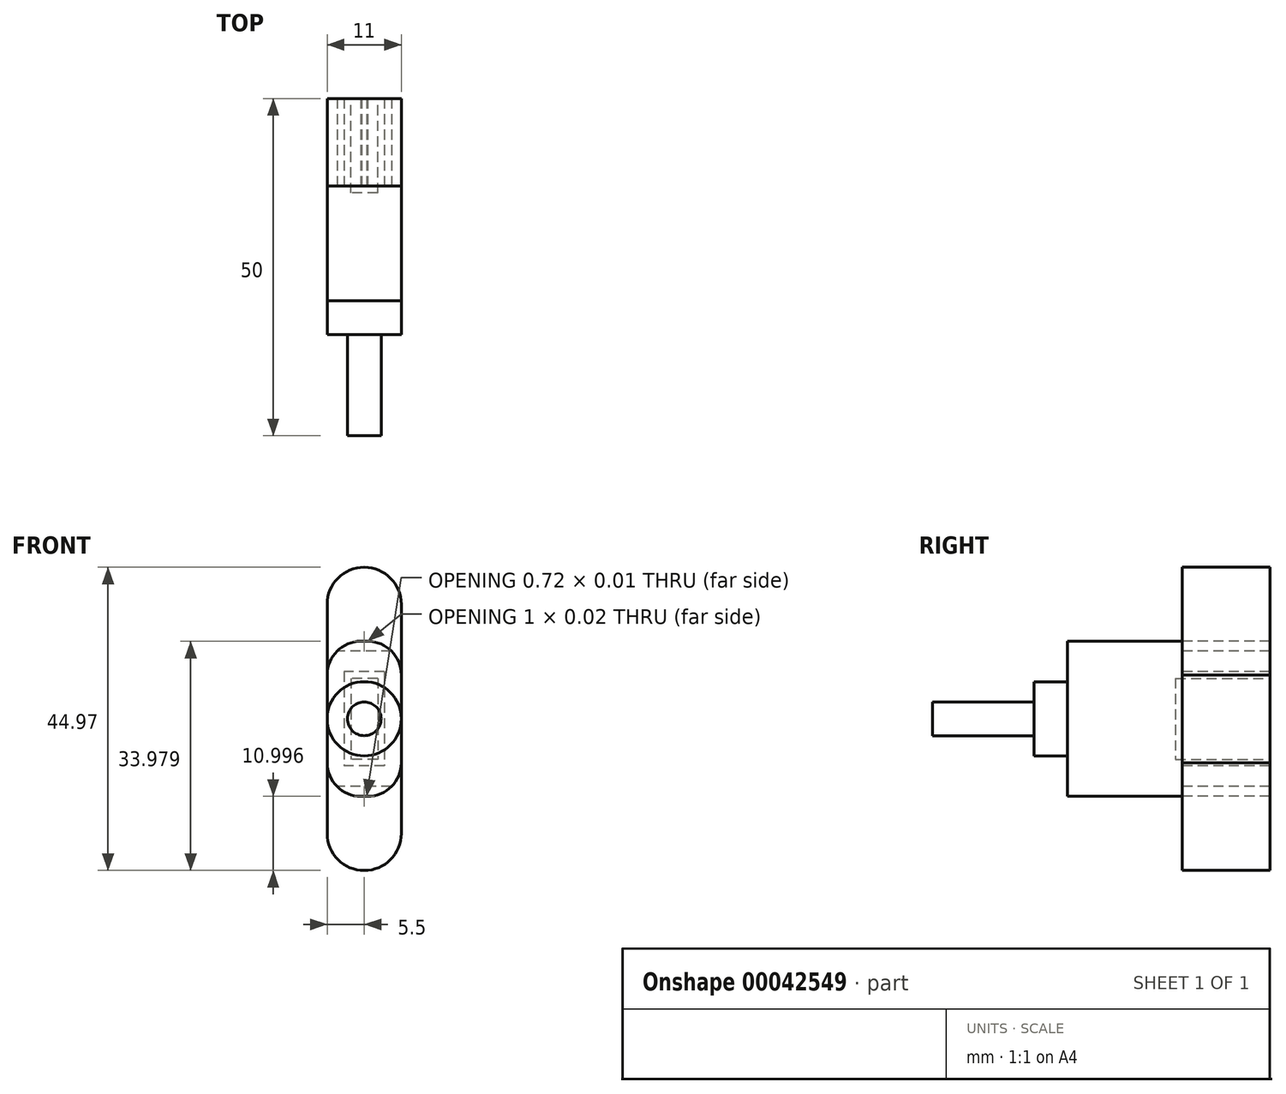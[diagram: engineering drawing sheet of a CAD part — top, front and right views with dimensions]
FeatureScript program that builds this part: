
annotation { "Feature Type Name" : "Feature", "Feature Type Description" : "" }
export const myFeature = defineFeature(function(context is Context, id is Id, definition is map)
    precondition{}
    {
        {
            var Q0;
            Q0=qCreatedBy(makeId("Front.planeOp"),FACE);
            var sketch = newSketch(context, id + "F0", { "sketchPlane" : qUnion([Q0])});
            skCircle(sketch, "E0", {"center": v(0, 0) * mm, "radius": 5.5 * mm});
            skSolve(sketch);
        }
        {
            var Q0;
            Q0 = qSketchRegion(id + "F0", true);
            extrude(context, id + "F1", {"entities" : qUnion([Q0]), "depth" : 5 * mm});
        }
        {
            var Q0;
            Q0=makeQuery(id+"F1.opExtrude","CAP_FACE",FACE,{"disambiguationData":[OSD([sQuery(id+"F0.wireOp",EDGE,"E0")])],"isStart":false});
            var sketch = newSketch(context, id + "F2", { "sketchPlane" : qUnion([Q0])});
            skCircle(sketch, "E1", {"center": v(0, 0) * mm, "radius": 2.5 * mm});
            skSolve(sketch);
        }
        {
            var Q0;
            Q0 = qSketchRegion(id + "F2", true);
            extrude(context, id + "F3", {"entities" : qUnion([Q0]), "operationType" : NewBodyOperationType.ADD, "depth" : 15 * mm});
        }
        {
            var Q0;
            Q0=makeQuery(id+"F1.opExtrude","CAP_FACE",FACE,{"disambiguationData":[OSD([sQuery(id+"F0.wireOp",EDGE,"E0")])],"isStart":true});
            var sketch = newSketch(context, id + "F4", { "sketchPlane" : qUnion([Q0])});
            skLineSegment(sketch, "E2", {"start": v(0, 0) * mm, "end": v(5.5, 0) * mm});
            skLineSegment(sketch, "E3", {"start": v(-5.5, 0) * mm, "end": v(0, 0) * mm});
            skLineSegment(sketch, "E4", {"start": v(0, 0) * mm, "end": v(0, 5.5) * mm});
            skLineSegment(sketch, "E5", {"start": v(0, 0) * mm, "end": v(0, -5.5) * mm});
            skLineSegment(sketch, "E6", {"start": v(0, -5.5) * mm, "end": v(0, -11.5) * mm});
            skLineSegment(sketch, "E7", {"start": v(0, 5.5) * mm, "end": v(0, 11.5) * mm});
            skLineSegment(sketch, "E8", {"start": v(0, 11.5) * mm, "end": v(5.5, 11.5) * mm});
            skLineSegment(sketch, "E9", {"start": v(5.5, 11.5) * mm, "end": v(5.5, -11.5) * mm});
            skLineSegment(sketch, "E10", {"start": v(5.5, -11.5) * mm, "end": v(0, -11.5) * mm});
            skLineSegment(sketch, "E11", {"start": v(0, 11.5) * mm, "end": v(-5.5, 11.5) * mm});
            skLineSegment(sketch, "E12", {"start": v(-5.5, 11.5) * mm, "end": v(-5.5, -11.5) * mm});
            skLineSegment(sketch, "E13", {"start": v(0, -11.5) * mm, "end": v(-5.5, -11.5) * mm});
            skSolve(sketch);
        }
        {
            var Q0;
            Q0 = qSketchRegion(id + "F4", true);
            extrude(context, id + "F5", {"entities" : qUnion([Q0]), "operationType" : NewBodyOperationType.ADD, "depth" : 17 * mm});
        }
        {
            var Q0;
            Q0=makeQuery(id+"F5.opExtrude","SWEPT_EDGE",EDGE,{"disambiguationData":[OSD([sQuery(id+"F4.wireOp",EDGE,"E9"),sQuery(id+"F4.wireOp",EDGE,"E10")])]});
            var Q1;
            Q1=makeQuery(id+"F5.opExtrude","SWEPT_EDGE",EDGE,{"disambiguationData":[OSD([sQuery(id+"F4.wireOp",EDGE,"E12"),sQuery(id+"F4.wireOp",EDGE,"E13")])]});
            var Q2;
            Q2=makeQuery(id+"F5.opExtrude","SWEPT_EDGE",EDGE,{"disambiguationData":[OSD([sQuery(id+"F4.wireOp",EDGE,"E11"),sQuery(id+"F4.wireOp",EDGE,"E12")])]});
            var Q3;
            Q3=makeQuery(id+"F5.opExtrude","SWEPT_EDGE",EDGE,{"disambiguationData":[OSD([sQuery(id+"F4.wireOp",EDGE,"E8"),sQuery(id+"F4.wireOp",EDGE,"E9")])]});
            fillet(context, id + "F6", {"entities" : qUnion([Q0, Q1, Q2, Q3]), "radius" : 5 * mm, "tangentPropagation" : true, "allowEdgeOverflow" : false});
        }
        {
            var Q0;
            Q0=makeQuery(id+"F5.opExtrude","CAP_FACE",FACE,{"disambiguationData":[OSD([sQuery(id+"F4.wireOp",EDGE,"E8"),sQuery(id+"F4.wireOp",EDGE,"E9"),sQuery(id+"F4.wireOp",EDGE,"E10"),sQuery(id+"F4.wireOp",EDGE,"E11"),sQuery(id+"F4.wireOp",EDGE,"E12"),sQuery(id+"F4.wireOp",EDGE,"E13")])],"isStart":false});
            var sketch = newSketch(context, id + "F7", { "sketchPlane" : qUnion([Q0])});
            skLineSegment(sketch, "E14.bottom", {"start": v(-3, 7) * mm, "end": v(3, 7) * mm});
            skLineSegment(sketch, "E14.top", {"start": v(-3, -7) * mm, "end": v(3, -7) * mm});
            skLineSegment(sketch, "E14.left", {"start": v(-3, 7) * mm, "end": v(-3, -7) * mm});
            skLineSegment(sketch, "E14.right", {"start": v(3, 7) * mm, "end": v(3, -7) * mm});
            skSolve(sketch);
        }
        {
            var Q0;
            Q0 = qSketchRegion(id + "F7", true);
            extrude(context, id + "F8", {"entities" : qUnion([Q0]), "operationType" : NewBodyOperationType.ADD, "depth" : 13 * mm});
        }
        {
            var Q0;
            Q0=makeQuery(id+"F8.opExtrude","CAP_FACE",FACE,{"disambiguationData":[OSD([sQuery(id+"F7.wireOp",EDGE,"E14.bottom"),sQuery(id+"F7.wireOp",EDGE,"E14.top"),sQuery(id+"F7.wireOp",EDGE,"E14.left"),sQuery(id+"F7.wireOp",EDGE,"E14.right")])],"isStart":false});
            var sketch = newSketch(context, id + "F9", { "sketchPlane" : qUnion([Q0])});
            skLineSegment(sketch, "E15.bottom", {"start": v(-2, 6) * mm, "end": v(2, 6) * mm});
            skLineSegment(sketch, "E15.top", {"start": v(-2, -6) * mm, "end": v(2, -6) * mm});
            skLineSegment(sketch, "E15.left", {"start": v(-2, 6) * mm, "end": v(-2, -6) * mm});
            skLineSegment(sketch, "E15.right", {"start": v(2, 6) * mm, "end": v(2, -6) * mm});
            skSolve(sketch);
        }
        {
            var Q0;
            Q0 = qSketchRegion(id + "F9", true);
            extrude(context, id + "F10", {"entities" : qUnion([Q0]), "operationType" : NewBodyOperationType.REMOVE, "oppositeDirection" : true, "depth" : 14 * mm});
        }
        {
            var Q0;
            Q0=makeQuery(id+"F5.opExtrude","CAP_FACE",FACE,{"disambiguationData":[OSD([sQuery(id+"F4.wireOp",EDGE,"E8"),sQuery(id+"F4.wireOp",EDGE,"E9"),sQuery(id+"F4.wireOp",EDGE,"E10"),sQuery(id+"F4.wireOp",EDGE,"E11"),sQuery(id+"F4.wireOp",EDGE,"E12"),sQuery(id+"F4.wireOp",EDGE,"E13")])],"isStart":false});
            var sketch = newSketch(context, id + "F11", { "sketchPlane" : qUnion([Q0])});
            skCircle(sketch, "E16", {"center": v(0, 16.98) * mm, "radius": 5.5 * mm});
            skPoint(sketch, "E16.centerSnap0", {"position": v(0, 11.5) * mm});
            skCircle(sketch, "E17", {"center": v(0, -16.99) * mm, "radius": 5.5 * mm});
            skPoint(sketch, "E17.centerSnap0", {"position": v(0, -11.5) * mm});
            skLineSegment(sketch, "E18", {"start": v(0, 16.98) * mm, "end": v(5.5, 16.98) * mm});
            skLineSegment(sketch, "E19", {"start": v(0, -16.99) * mm, "end": v(5.5, -16.99) * mm});
            skLineSegment(sketch, "E20", {"start": v(5.5, 16.98) * mm, "end": v(5.5, -16.99) * mm});
            skLineSegment(sketch, "E21", {"start": v(0, 16.98) * mm, "end": v(-5.5, 16.98) * mm});
            skLineSegment(sketch, "E22", {"start": v(0, -16.99) * mm, "end": v(-5.5, -16.99) * mm});
            skLineSegment(sketch, "E23", {"start": v(-5.5, 16.98) * mm, "end": v(-5.5, -16.99) * mm});
            skLineSegment(sketch, "E24", {"start": v(-4.04, 10.04) * mm, "end": v(4.04, 10.04) * mm});
            skLineSegment(sketch, "E25", {"start": v(-4.04, -10.04) * mm, "end": v(4.04, -10.04) * mm});
            skSolve(sketch);
        }
        {
            var Q0;
            {var subQ1=sQuery(id+"F11.wireOp",EDGE,"E18");Q0=makeQuery(id+"F11.imprint","IMPRINT",FACE,{"disambiguationData":[TD([[makeQuery(id+"F11.imprint","IMPRINT",EDGE,{"derivedFrom":subQ1}),1.0]])]});}
            var Q1;
            {var subQ8=sQuery(id+"F11.wireOp",EDGE,"E18");Q1=makeQuery(id+"F11.imprint","IMPRINT",FACE,{"disambiguationData":[TD([[makeQuery(id+"F11.imprint","IMPRINT",EDGE,{"derivedFrom":subQ8}),-1.0]])]});}
            var Q2;
            {var subQ0=sQuery(id+"F4.wireOp",EDGE,"E8");var subQ1=sQuery(id+"F4.wireOp",EDGE,"E9");var subQ2=sQuery(id+"F4.wireOp",EDGE,"E11");var subQ3=makeQuery(id+"F6.opFillet","BLEND_EDGE",EDGE,{"blendedFrom":[makeQuery(id+"F5.opExtrude","SWEPT_EDGE",EDGE,{"disambiguationData":[OSD([subQ0,subQ1])]}),makeQuery(id+"F5.opExtrude","CAP_FACE",FACE,{"disambiguationData":[OSD([subQ0,subQ1,sQuery(id+"F4.wireOp",EDGE,"E10"),subQ2,sQuery(id+"F4.wireOp",EDGE,"E12"),sQuery(id+"F4.wireOp",EDGE,"E13")])],"isStart":false})],"blendedInto":[makeQuery(id+"F5.opExtrude","CAP_FACE",FACE,{"disambiguationData":[OSD([subQ0,subQ1,sQuery(id+"F4.wireOp",EDGE,"E10"),subQ2,sQuery(id+"F4.wireOp",EDGE,"E12"),sQuery(id+"F4.wireOp",EDGE,"E13")])],"isStart":false})]});Q2=makeQuery(id+"F11.imprint","IMPRINT",FACE,{"disambiguationData":[TD([[makeQuery(id+"F11.imprint","IMPRINT",EDGE,{"derivedFrom":subQ3}),-1.0]])]});}
            var Q3;
            {var subQ0=sQuery(id+"F4.wireOp",EDGE,"E11");var subQ1=sQuery(id+"F4.wireOp",EDGE,"E12");var subQ2=sQuery(id+"F4.wireOp",EDGE,"E8");var subQ3=makeQuery(id+"F6.opFillet","BLEND_EDGE",EDGE,{"blendedFrom":[makeQuery(id+"F5.opExtrude","SWEPT_EDGE",EDGE,{"disambiguationData":[OSD([subQ0,subQ1])]}),makeQuery(id+"F5.opExtrude","CAP_FACE",FACE,{"disambiguationData":[OSD([subQ2,sQuery(id+"F4.wireOp",EDGE,"E9"),sQuery(id+"F4.wireOp",EDGE,"E10"),subQ0,subQ1,sQuery(id+"F4.wireOp",EDGE,"E13")])],"isStart":false})],"blendedInto":[makeQuery(id+"F5.opExtrude","CAP_FACE",FACE,{"disambiguationData":[OSD([subQ2,sQuery(id+"F4.wireOp",EDGE,"E9"),sQuery(id+"F4.wireOp",EDGE,"E10"),subQ0,subQ1,sQuery(id+"F4.wireOp",EDGE,"E13")])],"isStart":false})]});Q3=makeQuery(id+"F11.imprint","IMPRINT",FACE,{"disambiguationData":[TD([[makeQuery(id+"F11.imprint","IMPRINT",EDGE,{"derivedFrom":subQ3}),-1.0]])]});}
            var Q4;
            {var subQ4=sQuery(id+"F11.wireOp",EDGE,"E20");var subQ5=sQuery(id+"F11.wireOp",EDGE,"E17");var subQ6=makeQuery(id+"F11.imprint","INTERSECT",VERTEX,{"derivedFrom":[subQ5,sQuery(id+"F11.wireOp",EDGE,"E19"),subQ4]});Q4=makeQuery(id+"F11.imprint","IMPRINT",FACE,{"disambiguationData":[TD([[makeQuery(id+"F11.imprint","IMPRINT",EDGE,{"disambiguationData":[TD([[subQ6,-1.0]])],"derivedFrom":subQ5}),-1.0]])]});}
            var Q5;
            {var subQ3=sQuery(id+"F11.wireOp",EDGE,"E17");var subQ7=sQuery(id+"F11.wireOp",EDGE,"E23");var subQ8=makeQuery(id+"F11.imprint","INTERSECT",VERTEX,{"derivedFrom":[subQ3,sQuery(id+"F11.wireOp",EDGE,"E22"),subQ7]});Q5=makeQuery(id+"F11.imprint","IMPRINT",FACE,{"disambiguationData":[TD([[makeQuery(id+"F11.imprint","IMPRINT",EDGE,{"disambiguationData":[TD([[subQ8,1.0]])],"derivedFrom":subQ3}),-1.0]])]});}
            var Q6;
            {var subQ4=sQuery(id+"F11.wireOp",EDGE,"E19");Q6=makeQuery(id+"F11.imprint","IMPRINT",FACE,{"disambiguationData":[TD([[makeQuery(id+"F11.imprint","IMPRINT",EDGE,{"derivedFrom":subQ4}),1.0]])]});}
            var Q7;
            {var subQ1=sQuery(id+"F11.wireOp",EDGE,"E19");Q7=makeQuery(id+"F11.imprint","IMPRINT",FACE,{"disambiguationData":[TD([[makeQuery(id+"F11.imprint","IMPRINT",EDGE,{"derivedFrom":subQ1}),-1.0]])]});}
            var Q8;
            {var subQ13=sQuery(id+"F11.wireOp",EDGE,"E25");Q8=makeQuery(id+"F11.imprint","IMPRINT",FACE,{"disambiguationData":[TD([[makeQuery(id+"F11.imprint","IMPRINT",EDGE,{"derivedFrom":subQ13}),-1.0]])]});}
            var Q9;
            {var subQ6=sQuery(id+"F11.wireOp",EDGE,"E24");Q9=makeQuery(id+"F11.imprint","IMPRINT",FACE,{"disambiguationData":[TD([[makeQuery(id+"F11.imprint","IMPRINT",EDGE,{"derivedFrom":subQ6}),1.0]])]});}
            extrude(context, id + "F12", {"entities" : qUnion([Q0, Q1, Q2, Q3, Q4, Q5, Q6, Q7, Q8, Q9]), "depth" : 13 * mm});
        }
    });
